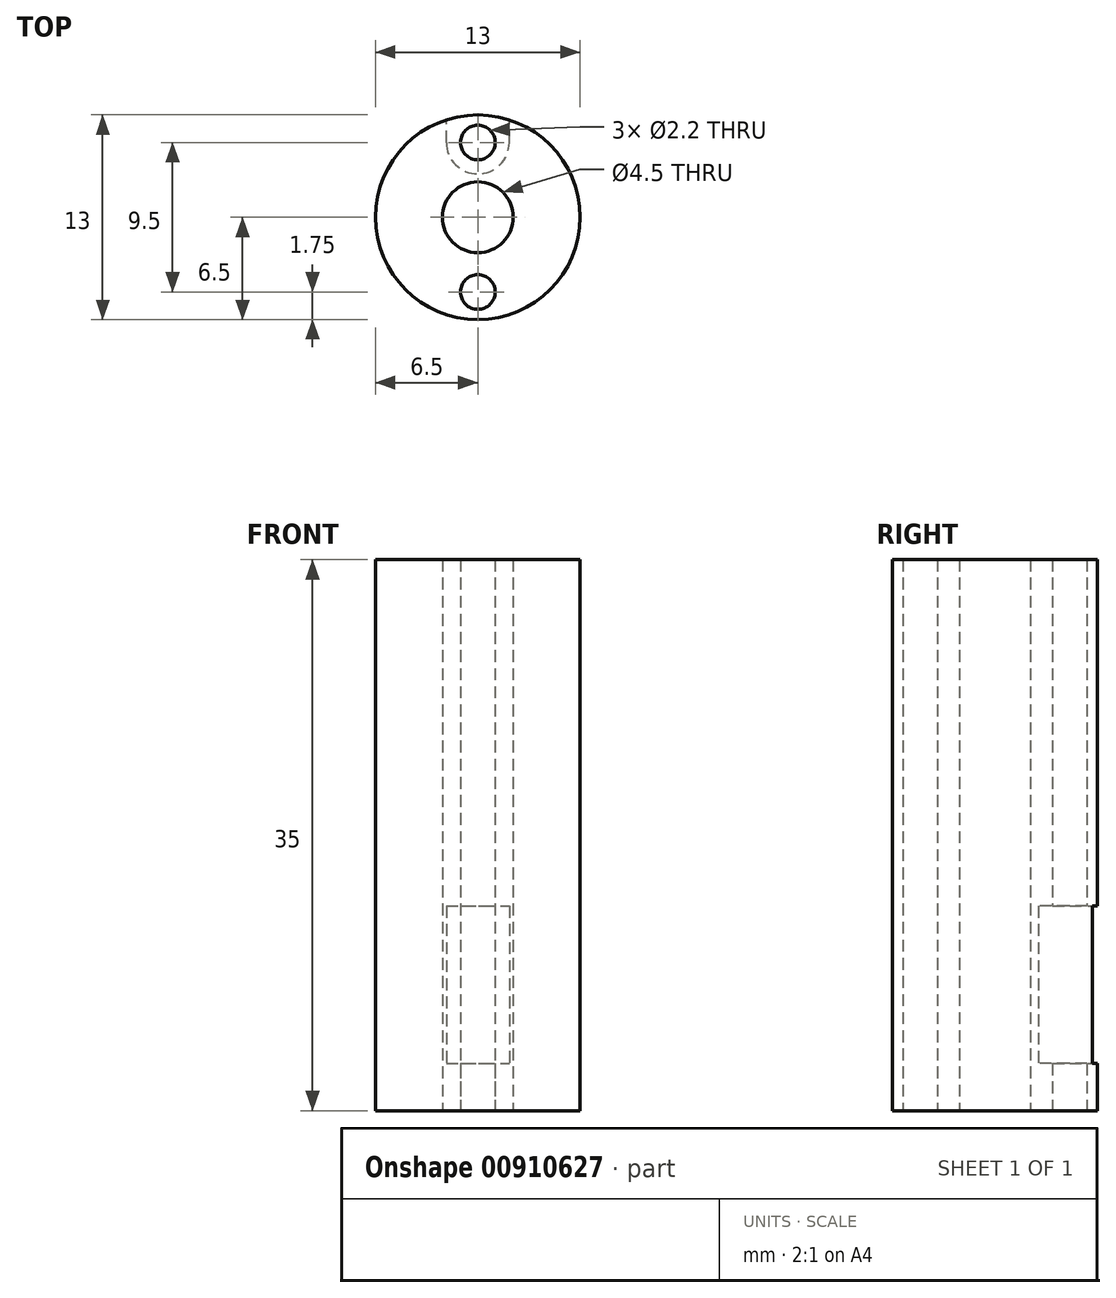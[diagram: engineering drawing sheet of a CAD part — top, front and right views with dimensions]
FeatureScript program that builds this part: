
annotation { "Feature Type Name" : "Feature", "Feature Type Description" : "" }
export const myFeature = defineFeature(function(context is Context, id is Id, definition is map)
    precondition{}
    {
        {
            var Q0;
            Q0=qCreatedBy(makeId("Top.planeOp"),FACE);
            var sketch = newSketch(context, id + "F0", { "sketchPlane" : qUnion([Q0])});
            skCircle(sketch, "E0", {"center": v(0, 0) * mm, "radius": 6.5 * mm});
            skCircle(sketch, "E1", {"center": v(0, 0) * mm, "radius": 2.25 * mm});
            skSolve(sketch);
        }
        {
            var Q0;
            Q0 = qSketchRegion(id + "F0", true);
            extrude(context, id + "F1", {"entities" : qUnion([Q0]), "depth" : 35 * mm, "offsetDistance" : 25 * mm});
        }
        {
            var Q0;
            Q0=makeQuery(id+"F1.opExtrude","CAP_FACE",FACE,{"disambiguationData":[OSD([sQuery(id+"F0.wireOp",EDGE,"E0"),sQuery(id+"F0.wireOp",EDGE,"E1")])],"isStart":true});
            var sketch = newSketch(context, id + "F2", { "sketchPlane" : qUnion([Q0])});
            skPoint(sketch, "E2", {"position": v(0, 4.75) * mm});
            skLineSegment(sketch, "E3", {"start": v(0, 0) * mm, "end": v(-6.5, 0) * mm, "construction": true});
            skPoint(sketch, "E4.MirrorP", {"position": v(0, -4.75) * mm});
            skSolve(sketch);
        }
        {
            var Q0;
            Q0=sQuery(id+"F2.wireOp",VERTEX,"E4.MirrorP");
            var Q1;
            Q1=sQuery(id+"F2.wireOp",VERTEX,"E2");
            var Q2;
            Q2=makeQuery(id+"F1.opExtrude","SWEPT_BODY",BODY,{"disambiguationData":[OSD([sQuery(id+"F0.wireOp",EDGE,"E0"),sQuery(id+"F0.wireOp",EDGE,"E1")])]});
            hole(context, id + "F3", {"style" : HoleStyle.SIMPLE, "endStyle" : HoleEndStyle.THROUGH, "holeDiameter" : 2.2 * mm, "majorDiameter" : 5 * mm, "isTappedThrough" : true, "tappedDepth" : 12 * mm, "tapClearance" : 3, "locations" : qUnion([Q0, Q1]), "scope" : qUnion([Q2])});
        }
        {
            var Q0;
            Q0=makeQuery(id+"F1.opExtrude","CAP_FACE",FACE,{"disambiguationData":[OSD([sQuery(id+"F0.wireOp",EDGE,"E0"),sQuery(id+"F0.wireOp",EDGE,"E1")])],"isStart":true});
            var sketch = newSketch(context, id + "F4", { "sketchPlane" : qUnion([Q0])});
            skCircle(sketch, "E5", {"center": v(0, -4.75) * mm, "radius": 1.75 * mm});
            skCircle(sketch, "E6", {"center": v(0, 4.75) * mm, "radius": 1.75 * mm});
            skSolve(sketch);
        }
        {
            var Q0;
            {var subQ1=sQuery(id+"F4.wireOp",EDGE,"E5");Q0=makeQuery(id+"F4.imprint","IMPRINT",FACE,{"disambiguationData":[TD([[makeQuery(id+"F4.imprint","IMPRINT",EDGE,{"derivedFrom":subQ1}),-1.0]])]});}
            cPlane(context, id + "F5", {"entities" : qUnion([Q0]), "cplaneType" : CPlaneType.OFFSET, "offset" : 3 * mm, "oppositeDirection" : true, "width" : 150 * mm, "height" : 150 * mm});
        }
        {
            var Q0;
            Q0=qCreatedBy(id+"F5.planeOp",FACE);
            var sketch = newSketch(context, id + "F6", { "sketchPlane" : qUnion([Q0])});
            skArc(sketch, "E7", {"start": v(2, -4.75) * mm, "mid": v(0, -2.75) * mm, "end": v(-2, -4.75) * mm});
            skLineSegment(sketch, "E8", {"start": v(2, -4.75) * mm, "end": v(2, -6.75) * mm});
            skLineSegment(sketch, "E9", {"start": v(-2, -4.75) * mm, "end": v(-2, -6.75) * mm});
            skLineSegment(sketch, "E10", {"start": v(2, -6.75) * mm, "end": v(-2, -6.75) * mm});
            skSolve(sketch);
        }
        {
            var Q0;
            Q0 = qSketchRegion(id + "F6", true);
            extrude(context, id + "F7", {"entities" : qUnion([Q0]), "operationType" : NewBodyOperationType.REMOVE, "oppositeDirection" : true, "depth" : 10 * mm, "offsetDistance" : 25 * mm});
        }
    });
